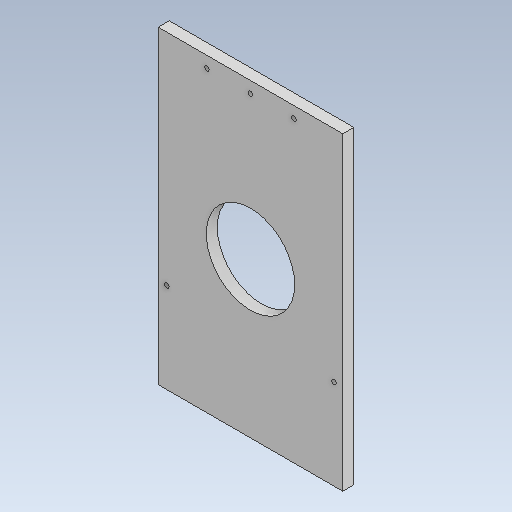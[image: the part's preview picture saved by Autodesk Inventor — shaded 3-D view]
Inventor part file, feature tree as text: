
AUTODESK INVENTOR PART (.ipt)
format: ipt  version: 2021.2 (Build 252289000, 289)  size: 125,440 bytes
history: native  units: in
note: dims shown in document units (in); Inventor stores cm internally (conversion verified against a paired STEP export)
features: sketch x4, extrude x2, hole x2
ambient origin geometry x8: Origin, YZ Plane, XZ Plane, XY Plane, X Axis, Y Axis, Z Axis, Center Point
bodies: Solid1 (feature_tree)
feature tree (8):
  extrude  "Extrusion1"  Depth=7.0in
  extrude  "CenterHole"  Depth=0.25in
  hole  "TopThreeHoles"  [1 undecoded]
  hole  "Hole3"  [1 undecoded]
  sketch  "Sketch2"  dims[d0=4.1732in d1=7.0in]
  sketch  "Sketch5"  dims[d2=0.25in d3=0.0in d26=2.0in]
  sketch  "Sketch6"  dims[d27=0.0in d28=0.0in d29=0.2559in]
  sketch  "Sketch7"  dims[d30=0.9843in d31=0.9843in d32=0.104in d33=0.276in d34=0.279in d35=0.25in d36=0.5635in d37=1.0in d38=0.8108in d39=4.9606in d40=0.1969in d41=0.1969in d42=0.104in d43=0.276in d44=0.279in d45=0.25in d46=0.5635in d47=1.0in d48=0.8108in]
note: 2 required parameter values undecoded (feature->parameter linkage not recoverable at this tier; creation-order binding heuristic only, values carry confidence <= 0.55)
